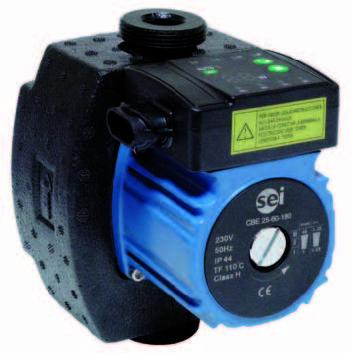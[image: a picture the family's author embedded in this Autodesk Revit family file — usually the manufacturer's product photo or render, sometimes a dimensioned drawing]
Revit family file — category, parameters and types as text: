
# Revit family: CBE_25-60_180-AC52102
name_source: partatom
category: Aparatos eléctricos
revit_build: Autodesk Revit 2016 (Build: 20150220_1215(x64)
units: mm (PartAtom-declared; Revit-internal decimal feet)

## family parameters
Compartido = No
Corte con vacíos al cargar = No
Cota de conector redondo = Diámetro de uso
Mantener orientación de anotación = No
Número OmniClass = 23.80.00.00
Punto de cálculo de habitación = No
Se basa en plano de trabajo = No
Siempre vertical = Sí
Tipo de pieza = Caja de conexiones
Título OmniClass = Electric Power and Lighting

## types (2) — shared parameters
Fabricante = SALVADOR ESCODA
Protección = 6,35 mm (1/4")
URL = www.salvadorescoda.com
zero-valued in all types: Costo

## per-type parameters (varying)
| type | Aislamiento | Caudal | Conexión rácores | Código de montaje | Descripción | Dimensiones Unidad Interior | Imagen de tipo | Modelo | Motor | Máx. presión trabajo | Peso | Presión disponible | Rango temperatura agua | Temperatura ambiente |
| MVD-22T2 | 35 dB(A) |  |  | CL23370 | CONDUCTO BAJA SILUETA | 700 x 210 x 500 mm | <Ninguno> | MVD-22T2/DHN1-DA5 | 521 m3/h | 2,2kW / 39W | 17,5 kg neto |  | 2,6kW / 39W | DC / WZDK100-38GS |
| CBE | 59 dB(A) | 1 m3/h | G1 1/2" DN | AC52102 | BOMBA CIRCULADORA ELECTRONICA CON AISLAMIENTO | 180 x 105 x 100 mm | SEI_CBE.jpg | CBE 25-60_180 | 2 polos, 1x230V - 50Hz | 10 bar | 3,5 Kgs | 5 m.c.a. | 2º a 110 ºC | Hasta 40ºC |
